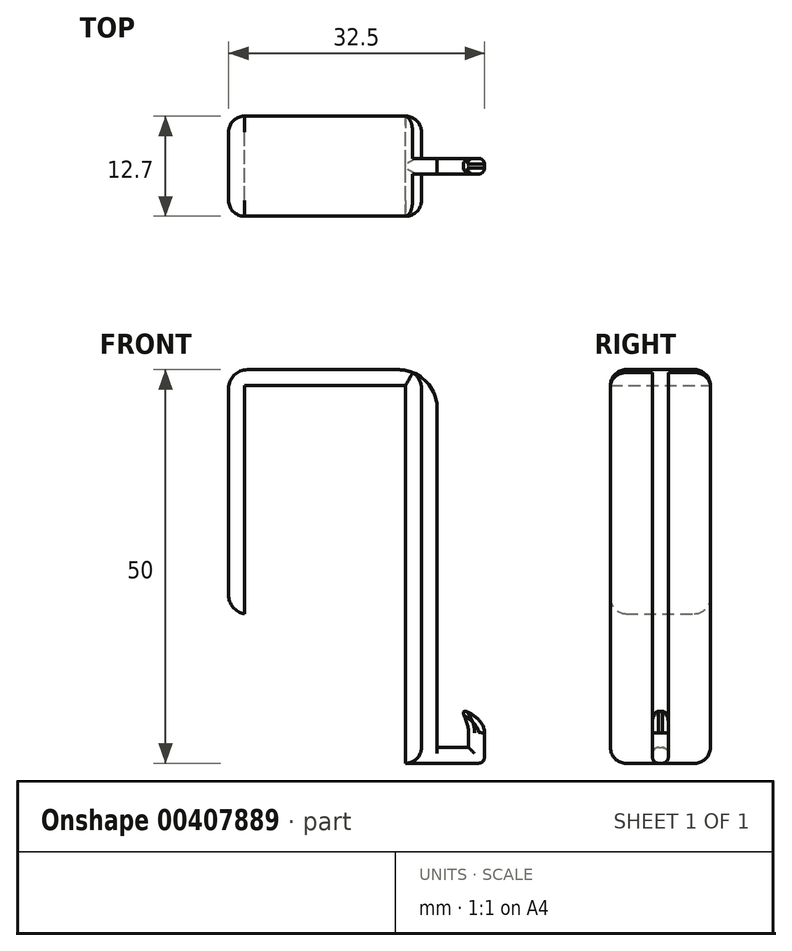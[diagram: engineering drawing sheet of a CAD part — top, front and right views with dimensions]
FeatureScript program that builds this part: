
annotation { "Feature Type Name" : "Feature", "Feature Type Description" : "" }
export const myFeature = defineFeature(function(context is Context, id is Id, definition is map)
    precondition{}
    {
        {
            var Q0;
            Q0=qCreatedBy(makeId("Front.planeOp"),FACE);
            var sketch = newSketch(context, id + "F0", { "sketchPlane" : qUnion([Q0])});
            skLineSegment(sketch, "E0", {"start": v(0, -8.46) * mm, "end": v(0, 22.54) * mm});
            skLineSegment(sketch, "E1", {"start": v(0, 22.54) * mm, "end": v(24.5, 22.54) * mm});
            skLineSegment(sketch, "E2", {"start": v(24.5, 22.54) * mm, "end": v(24.5, -27.46) * mm});
            skLineSegment(sketch, "E3", {"start": v(24.5, -27.46) * mm, "end": v(22.5, -27.46) * mm});
            skLineSegment(sketch, "E4", {"start": v(22.5, -27.46) * mm, "end": v(22.5, 20.54) * mm});
            skLineSegment(sketch, "E5", {"start": v(22.5, 20.54) * mm, "end": v(2, 20.54) * mm});
            skLineSegment(sketch, "E6", {"start": v(2, 20.54) * mm, "end": v(2, -8.46) * mm});
            skLineSegment(sketch, "E7", {"start": v(2, -8.46) * mm, "end": v(0, -8.46) * mm});
            skSolve(sketch);
        }
        {
            var Q0;
            Q0=makeQuery(id+"F0.imprint","IMPRINT",FACE,{"disambiguationData":[TD([[makeQuery(id+"F0.imprint","IMPRINT",EDGE,{"derivedFrom":sQuery(id+"F0.wireOp",EDGE,"E0")}),-1.0]])]});
            extrude(context, id + "F1", {"entities" : qUnion([Q0]), "endBound" : BoundingType.SYMMETRIC, "depth" : 12.7 * mm});
        }
        {
            var Q0;
            Q0=qCreatedBy(makeId("Front.planeOp"),FACE);
            var sketch = newSketch(context, id + "F2", { "sketchPlane" : qUnion([Q0])});
            skLineSegment(sketch, "E8", {"start": v(24.5, 22.54) * mm, "end": v(24.5, -22.46) * mm});
            skLineSegment(sketch, "E9", {"start": v(24.5, -22.46) * mm, "end": v(24.5, -27.46) * mm});
            skLineSegment(sketch, "E10", {"start": v(24.5, -27.46) * mm, "end": v(32.5, -27.46) * mm});
            skLineSegment(sketch, "E11", {"start": v(32.5, -27.46) * mm, "end": v(32.5, -23.58) * mm});
            skLineSegment(sketch, "E12", {"start": v(32.5, -23.58) * mm, "end": v(30.5, -23.58) * mm});
            skLineSegment(sketch, "E13", {"start": v(30.5, -23.58) * mm, "end": v(30.5, -25.46) * mm});
            skLineSegment(sketch, "E14", {"start": v(30.5, -25.46) * mm, "end": v(26.5, -25.46) * mm});
            skLineSegment(sketch, "E15", {"start": v(26.5, -25.46) * mm, "end": v(26.5, -17.46) * mm});
            skLineSegment(sketch, "E16", {"start": v(26.5, -17.46) * mm, "end": v(26.5, 22.54) * mm});
            skLineSegment(sketch, "E17", {"start": v(26.5, 22.54) * mm, "end": v(24.5, 22.54) * mm});
            skFitSpline(sketch, "E18", {"points": [v(30.5, -23.58) * mm, v(29.9, -20.87) * mm, v(32.5, -23.58) * mm], "startDerivative": vector(0, 8.24) * mm, "endDerivative": vector(-0.3, -8.63) * mm});
            skSolve(sketch);
        }
        {
            var Q0;
            Q0=makeQuery(id+"F2.imprint","IMPRINT",FACE,{"disambiguationData":[TD([[makeQuery(id+"F2.imprint","IMPRINT",EDGE,{"derivedFrom":sQuery(id+"F2.wireOp",EDGE,"E8")}),1.0]])]});
            var Q1;
            Q1=makeQuery(id+"F2.imprint","IMPRINT",FACE,{"disambiguationData":[TD([[makeQuery(id+"F2.imprint","IMPRINT",EDGE,{"derivedFrom":sQuery(id+"F2.wireOp",EDGE,"E12")}),-1.0]])]});
            extrude(context, id + "F3", {"entities" : qUnion([Q0, Q1]), "operationType" : NewBodyOperationType.ADD, "endBound" : BoundingType.SYMMETRIC, "depth" : 2 * mm});
        }
        {
            var Q0;
            Q0=makeQuery(id+"F1.opExtrude","SWEPT_EDGE",EDGE,{"disambiguationData":[OSD([sQuery(id+"F0.wireOp",EDGE,"E0"),sQuery(id+"F0.wireOp",EDGE,"E1")])]});
            var Q1;
            Q1=makeQuery(id+"F1.opExtrude","SWEPT_EDGE",EDGE,{"disambiguationData":[OSD([sQuery(id+"F0.wireOp",EDGE,"E0"),sQuery(id+"F0.wireOp",EDGE,"E7")])]});
            var Q2;
            {var subQ1=sQuery(id+"F0.wireOp",EDGE,"E2");var subQ2=sQuery(id+"F0.wireOp",EDGE,"E1");Q2=makeQuery(id+"F3.boolean.opBoolean","SPLIT",EDGE,{"disambiguationData":[TD([makeQuery(id+"F1.opExtrude","CAP_FACE",FACE,{"disambiguationData":[OSD([sQuery(id+"F0.wireOp",EDGE,"E0"),subQ2,subQ1,sQuery(id+"F0.wireOp",EDGE,"E3"),sQuery(id+"F0.wireOp",EDGE,"E4"),sQuery(id+"F0.wireOp",EDGE,"E5"),sQuery(id+"F0.wireOp",EDGE,"E6"),sQuery(id+"F0.wireOp",EDGE,"E7")])],"isStart":false})])],"derivedFrom":makeQuery(id+"F1.opExtrude","SWEPT_EDGE",EDGE,{"disambiguationData":[OSD([subQ2,subQ1])]})});}
            var Q3;
            {var subQ1=sQuery(id+"F0.wireOp",EDGE,"E2");var subQ2=sQuery(id+"F0.wireOp",EDGE,"E1");Q3=makeQuery(id+"F3.boolean.opBoolean","SPLIT",EDGE,{"disambiguationData":[TD([makeQuery(id+"F1.opExtrude","CAP_FACE",FACE,{"disambiguationData":[OSD([sQuery(id+"F0.wireOp",EDGE,"E0"),subQ2,subQ1,sQuery(id+"F0.wireOp",EDGE,"E3"),sQuery(id+"F0.wireOp",EDGE,"E4"),sQuery(id+"F0.wireOp",EDGE,"E5"),sQuery(id+"F0.wireOp",EDGE,"E6"),sQuery(id+"F0.wireOp",EDGE,"E7")])],"isStart":true})])],"derivedFrom":makeQuery(id+"F1.opExtrude","SWEPT_EDGE",EDGE,{"disambiguationData":[OSD([subQ2,subQ1])]})});}
            fillet(context, id + "F4", {"entities" : qUnion([Q0, Q1, Q2, Q3]), "radius" : 2.4 * mm, "tangentPropagation" : true, "allowEdgeOverflow" : false});
        }
        {
            var Q0;
            Q0=makeQuery(id+"F3.opExtrude","CAP_EDGE",EDGE,{"disambiguationData":[OSD([sQuery(id+"F2.wireOp",EDGE,"E14")])],"isStart":false});
            var Q1;
            Q1=makeQuery(id+"F3.opExtrude","CAP_EDGE",EDGE,{"disambiguationData":[OSD([sQuery(id+"F2.wireOp",EDGE,"E13")])],"isStart":false});
            var Q2;
            Q2=makeQuery(id+"F3.opExtrude","CAP_EDGE",EDGE,{"disambiguationData":[OSD([sQuery(id+"F2.wireOp",EDGE,"E11")])],"isStart":false});
            var Q3;
            Q3=makeQuery(id+"F3.opExtrude","CAP_EDGE",EDGE,{"disambiguationData":[OSD([sQuery(id+"F2.wireOp",EDGE,"E18")])],"isStart":false});
            var Q4;
            Q4=makeQuery(id+"F3.opExtrude","CAP_EDGE",EDGE,{"disambiguationData":[OSD([sQuery(id+"F2.wireOp",EDGE,"E10")])],"isStart":false});
            var Q5;
            Q5=makeQuery(id+"F3.opExtrude","CAP_EDGE",EDGE,{"disambiguationData":[OSD([sQuery(id+"F2.wireOp",EDGE,"E18")])],"isStart":true});
            var Q6;
            Q6=makeQuery(id+"F3.opExtrude","CAP_EDGE",EDGE,{"disambiguationData":[OSD([sQuery(id+"F2.wireOp",EDGE,"E11")])],"isStart":true});
            var Q7;
            Q7=makeQuery(id+"F3.opExtrude","CAP_EDGE",EDGE,{"disambiguationData":[OSD([sQuery(id+"F2.wireOp",EDGE,"E14")])],"isStart":true});
            var Q8;
            Q8=makeQuery(id+"F3.opExtrude","CAP_EDGE",EDGE,{"disambiguationData":[OSD([sQuery(id+"F2.wireOp",EDGE,"E10")])],"isStart":true});
            var Q9;
            Q9=makeQuery(id+"F3.opExtrude","SWEPT_EDGE",EDGE,{"disambiguationData":[OSD([sQuery(id+"F2.wireOp",EDGE,"E10"),sQuery(id+"F2.wireOp",EDGE,"E11")])]});
            fillet(context, id + "F5", {"entities" : qUnion([Q0, Q1, Q2, Q3, Q4, Q5, Q6, Q7, Q8, Q9]), "radius" : .75 * mm, "tangentPropagation" : true, "allowEdgeOverflow" : false});
        }
        {
            var Q0;
            Q0=makeQuery(id+"F3.opExtrude","SWEPT_EDGE",EDGE,{"disambiguationData":[OSD([sQuery(id+"F2.wireOp",EDGE,"E16"),sQuery(id+"F2.wireOp",EDGE,"E17")])]});
            fillet(context, id + "F6", {"entities" : qUnion([Q0]), "radius" : 5 * mm, "tangentPropagation" : true, "allowEdgeOverflow" : false});
        }
        {
            var Q0;
            {var subQ0=sQuery(id+"F0.wireOp",EDGE,"E7");var subQ1=sQuery(id+"F0.wireOp",EDGE,"E0");Q0=makeQuery(id+"F4.opFillet","BLEND_EDGE",EDGE,{"blendedFrom":[makeQuery(id+"F1.opExtrude","SWEPT_EDGE",EDGE,{"disambiguationData":[OSD([subQ1,subQ0])]}),makeQuery(id+"F1.opExtrude","CAP_FACE",FACE,{"disambiguationData":[OSD([subQ1,sQuery(id+"F0.wireOp",EDGE,"E1"),sQuery(id+"F0.wireOp",EDGE,"E2"),sQuery(id+"F0.wireOp",EDGE,"E3"),sQuery(id+"F0.wireOp",EDGE,"E4"),sQuery(id+"F0.wireOp",EDGE,"E5"),sQuery(id+"F0.wireOp",EDGE,"E6"),subQ0])],"isStart":false})],"blendedInto":[makeQuery(id+"F1.opExtrude","CAP_FACE",FACE,{"disambiguationData":[OSD([subQ1,sQuery(id+"F0.wireOp",EDGE,"E1"),sQuery(id+"F0.wireOp",EDGE,"E2"),sQuery(id+"F0.wireOp",EDGE,"E3"),sQuery(id+"F0.wireOp",EDGE,"E4"),sQuery(id+"F0.wireOp",EDGE,"E5"),sQuery(id+"F0.wireOp",EDGE,"E6"),subQ0])],"isStart":false})]});}
            var Q1;
            Q1=makeQuery(id+"F1.opExtrude","CAP_EDGE",EDGE,{"disambiguationData":[OSD([sQuery(id+"F0.wireOp",EDGE,"E0")])],"isStart":false});
            var Q2;
            Q2=makeQuery(id+"F1.opExtrude","CAP_EDGE",EDGE,{"disambiguationData":[OSD([sQuery(id+"F0.wireOp",EDGE,"E2")])],"isStart":false});
            var Q3;
            Q3=makeQuery(id+"F1.opExtrude","CAP_EDGE",EDGE,{"disambiguationData":[OSD([sQuery(id+"F0.wireOp",EDGE,"E2")])],"isStart":true});
            var Q4;
            Q4=makeQuery(id+"F6.opFillet","BLEND_EDGE",EDGE,{"blendedFrom":[makeQuery(id+"F3.opExtrude","SWEPT_EDGE",EDGE,{"disambiguationData":[OSD([sQuery(id+"F2.wireOp",EDGE,"E16"),sQuery(id+"F2.wireOp",EDGE,"E17")])]}),makeQuery(id+"F1.opExtrude","CAP_FACE",FACE,{"disambiguationData":[OSD([sQuery(id+"F0.wireOp",EDGE,"E0"),sQuery(id+"F0.wireOp",EDGE,"E1"),sQuery(id+"F0.wireOp",EDGE,"E2"),sQuery(id+"F0.wireOp",EDGE,"E3"),sQuery(id+"F0.wireOp",EDGE,"E4"),sQuery(id+"F0.wireOp",EDGE,"E5"),sQuery(id+"F0.wireOp",EDGE,"E6"),sQuery(id+"F0.wireOp",EDGE,"E7")])],"isStart":true})],"blendedInto":[makeQuery(id+"F1.opExtrude","CAP_FACE",FACE,{"disambiguationData":[OSD([sQuery(id+"F0.wireOp",EDGE,"E0"),sQuery(id+"F0.wireOp",EDGE,"E1"),sQuery(id+"F0.wireOp",EDGE,"E2"),sQuery(id+"F0.wireOp",EDGE,"E3"),sQuery(id+"F0.wireOp",EDGE,"E4"),sQuery(id+"F0.wireOp",EDGE,"E5"),sQuery(id+"F0.wireOp",EDGE,"E6"),sQuery(id+"F0.wireOp",EDGE,"E7")])],"isStart":true})]});
            var Q5;
            Q5=makeQuery(id+"F1.opExtrude","SWEPT_EDGE",EDGE,{"disambiguationData":[OSD([sQuery(id+"F0.wireOp",EDGE,"E2"),sQuery(id+"F0.wireOp",EDGE,"E3")])]});
            var Q6;
            Q6=makeQuery(id+"F1.opExtrude","CAP_EDGE",EDGE,{"disambiguationData":[OSD([sQuery(id+"F0.wireOp",EDGE,"E3")])],"isStart":true});
            var Q7;
            Q7=makeQuery(id+"F1.opExtrude","CAP_EDGE",EDGE,{"disambiguationData":[OSD([sQuery(id+"F0.wireOp",EDGE,"E3")])],"isStart":false});
            fillet(context, id + "F7", {"entities" : qUnion([Q0, Q1, Q2, Q3, Q4, Q5, Q6, Q7]), "radius" : 2 * mm, "tangentPropagation" : true, "allowEdgeOverflow" : false});
        }
    });
